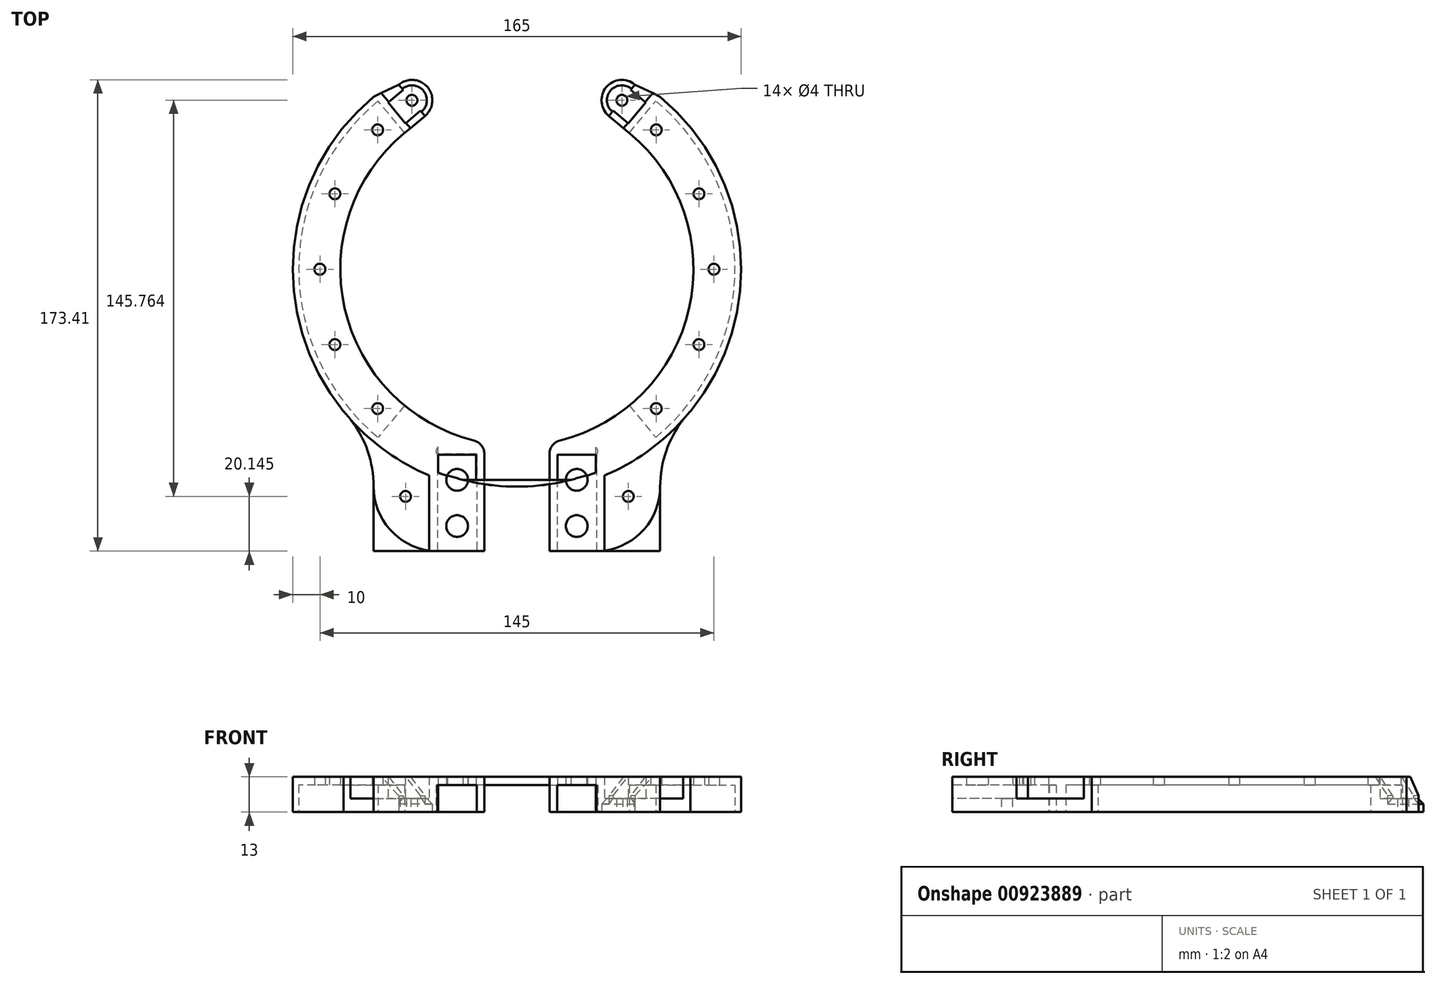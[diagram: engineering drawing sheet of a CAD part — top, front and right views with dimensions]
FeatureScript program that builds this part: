
annotation { "Feature Type Name" : "Feature", "Feature Type Description" : "" }
export const myFeature = defineFeature(function(context is Context, id is Id, definition is map)
    precondition{}
    {
        {
            var Q0;
            Q0=qCreatedBy(makeId("Top.planeOp"),FACE);
            var sketch = newSketch(context, id + "F0", { "sketchPlane" : qUnion([Q0])});
            skArc(sketch, "E0", {"start": v(-55.64, 25) * mm, "mid": v(-61, 0) * mm, "end": v(-55.64, -25) * mm});
            skArc(sketch, "E1.trimOffspring", {"start": v(55.64, -25) * mm, "mid": v(61, 0) * mm, "end": v(55.64, 25) * mm});
            skCircle(sketch, "E2", {"center": v(0, 0) * mm, "radius": 61 * mm});
            skCircle(sketch, "E3", {"center": v(0, 0) * mm, "radius": 65 * mm});
            skLineSegment(sketch, "E4", {"start": v(-41.53, 50) * mm, "end": v(-41.53, -50) * mm});
            skCircle(sketch, "E5", {"center": v(0, 0) * mm, "radius": 80 * mm});
            skLineSegment(sketch, "E6", {"start": v(-41.53, 50) * mm, "end": v(-51.12, 61.54) * mm});
            skLineSegment(sketch, "E7", {"start": v(-41.53, -50) * mm, "end": v(-51.12, -61.54) * mm});
            skArc(sketch, "E8", {"start": v(-46.33, -55.77) * mm, "mid": v(-72.5, 0) * mm, "end": v(-46.33, 55.77) * mm});
            skCircle(sketch, "E9", {"center": v(-72.5, 0) * mm, "radius": 2 * mm});
            skCircle(sketch, "E10.1.0", {"center": v(-66.98, -27.74) * mm, "radius": 2 * mm});
            skCircle(sketch, "E10.2.0", {"center": v(-51.27, -51.27) * mm, "radius": 2 * mm});
            skCircle(sketch, "E11.1.3.0", {"center": v(-27.74, -66.98) * mm, "radius": 2 * mm});
            skCircle(sketch, "E11.1.4.0", {"center": v(0, -72.5) * mm, "radius": 2 * mm});
            skCircle(sketch, "E11.1.5.0", {"center": v(27.74, -66.98) * mm, "radius": 2 * mm});
            skCircle(sketch, "E11.1.6.0", {"center": v(51.27, -51.27) * mm, "radius": 2 * mm});
            skCircle(sketch, "E11.1.7.0", {"center": v(66.98, -27.74) * mm, "radius": 2 * mm});
            skCircle(sketch, "E12.1.8.0", {"center": v(72.5, 0) * mm, "radius": 2 * mm});
            skCircle(sketch, "E12.1.9.0", {"center": v(66.98, 27.74) * mm, "radius": 2 * mm});
            skCircle(sketch, "E12.1.10.0", {"center": v(51.27, 51.27) * mm, "radius": 2 * mm});
            skCircle(sketch, "E12.1.11.0", {"center": v(27.74, 66.98) * mm, "radius": 2 * mm});
            skCircle(sketch, "E13.1.12.0", {"center": v(0, 72.5) * mm, "radius": 2 * mm});
            skCircle(sketch, "E13.1.13.0", {"center": v(-27.74, 66.98) * mm, "radius": 2 * mm});
            skCircle(sketch, "E13.1.14.0", {"center": v(-51.27, 51.27) * mm, "radius": 2 * mm});
            skCircle(sketch, "E13.1.15.0", {"center": v(-66.98, 27.74) * mm, "radius": 2 * mm});
            skLineSegment(sketch, "E14", {"start": v(-51.12, 61.54) * mm, "end": v(-43.43, 67.93) * mm});
            skLineSegment(sketch, "E15", {"start": v(-43.43, 67.93) * mm, "end": v(-33.84, 56.39) * mm});
            skLineSegment(sketch, "E16", {"start": v(-33.84, 56.39) * mm, "end": v(-41.53, 50) * mm});
            skArc(sketch, "E17", {"start": v(-43.43, 67.93) * mm, "mid": v(-32.86, 66.95) * mm, "end": v(-33.84, 56.39) * mm});
            skCircle(sketch, "E18", {"center": v(-38.63, 62.16) * mm, "radius": 2 * mm});
            skLineSegment(sketch, "E19.0", {"start": v(-35.44, 58.31) * mm, "end": v(-43.13, 51.92) * mm});
            skLineSegment(sketch, "E20.0", {"start": v(-49.52, 59.62) * mm, "end": v(-41.83, 66) * mm});
            skLineSegment(sketch, "E21", {"start": v(-51.12, 61.54) * mm, "end": v(-52.72, 63.46) * mm});
            skLineSegment(sketch, "E22", {"start": v(-51.12, -61.54) * mm, "end": v(-52.72, -63.46) * mm});
            skArc(sketch, "E23", {"start": v(-52.72, -63.46) * mm, "mid": v(-82.5, 0) * mm, "end": v(-52.72, 63.46) * mm});
            skLineSegment(sketch, "E24", {"start": v(-52.72, 63.46) * mm, "end": v(-43.43, 67.93) * mm});
            skLineSegment(sketch, "E25.bottom", {"start": v(22, -77.5) * mm, "end": v(-22, -77.5) * mm});
            skLineSegment(sketch, "E25.top", {"start": v(22, -94.5) * mm, "end": v(-22, -94.5) * mm});
            skLineSegment(sketch, "E25.left", {"start": v(22, -77.5) * mm, "end": v(22, -94.5) * mm});
            skLineSegment(sketch, "E25.right", {"start": v(-22, -77.5) * mm, "end": v(-22, -94.5) * mm});
            skPoint(sketch, "E25.middle", {"position": v(0, -86) * mm});
            skCircle(sketch, "E26", {"center": v(-22, -77.5) * mm, "radius": 4 * mm});
            skCircle(sketch, "E27", {"center": v(-22, -94.5) * mm, "radius": 4 * mm});
            skLineSegment(sketch, "E28.bottom", {"start": v(-15, -68.25) * mm, "end": v(-29, -68.25) * mm});
            skLineSegment(sketch, "E28.top", {"start": v(-15, -103.75) * mm, "end": v(-29, -103.75) * mm});
            skLineSegment(sketch, "E28.left", {"start": v(-15, -68.25) * mm, "end": v(-15, -103.75) * mm});
            skLineSegment(sketch, "E28.right", {"start": v(-29, -68.25) * mm, "end": v(-29, -103.75) * mm});
            skPoint(sketch, "E28.middle", {"position": v(-22, -86) * mm});
            skLineSegment(sketch, "E29.bottom", {"start": v(-29, -103.75) * mm, "end": v(-52.72, -103.75) * mm});
            skLineSegment(sketch, "E29.top", {"start": v(-29, -63.46) * mm, "end": v(-52.72, -63.46) * mm});
            skLineSegment(sketch, "E29.left", {"start": v(-29, -103.75) * mm, "end": v(-29, -63.46) * mm});
            skLineSegment(sketch, "E29.right", {"start": v(-52.72, -103.75) * mm, "end": v(-52.72, -63.46) * mm});
            skArc(sketch, "E30", {"start": v(-29, -103.75) * mm, "mid": v(-45.77, -96.8) * mm, "end": v(-52.72, -80.03) * mm});
            skLineSegment(sketch, "E31", {"start": v(-52.72, -80.03) * mm, "end": v(-29, -80.03) * mm, "construction": true});
            skArc(sketch, "E32", {"start": v(-52.72, -80.03) * mm, "mid": v(-55.58, -65.13) * mm, "end": v(-63.77, -52.34) * mm});
            skLineSegment(sketch, "E33", {"start": v(-15, -103.75) * mm, "end": v(-12, -103.75) * mm});
            skLineSegment(sketch, "E34", {"start": v(-12, -103.75) * mm, "end": v(-12, -63.88) * mm});
            skLineSegment(sketch, "E35.0", {"start": v(-14.75, -68) * mm, "end": v(-14.75, -103.75) * mm});
            skLineSegment(sketch, "E35.1", {"start": v(-14.75, -68) * mm, "end": v(-29.25, -68) * mm});
            skLineSegment(sketch, "E35.2", {"start": v(-29.25, -68) * mm, "end": v(-29.25, -103.75) * mm});
            skLineSegment(sketch, "E36.0", {"start": v(-32.25, -75.94) * mm, "end": v(-32.25, -103.53) * mm});
            skArc(sketch, "E37", {"start": v(-52.72, -63.46) * mm, "mid": v(-42.94, -70.45) * mm, "end": v(-32.25, -75.94) * mm});
            skLineSegment(sketch, "E38", {"start": v(-29.25, -103.75) * mm, "end": v(-40.98, -83.6) * mm, "construction": true});
            skLineSegment(sketch, "E39", {"start": v(-40.98, -83.6) * mm, "end": v(-52.72, -63.46) * mm, "construction": true});
            skCircle(sketch, "E40", {"center": v(-40.98, -83.6) * mm, "radius": 2 * mm});
            skLineSegment(sketch, "E41.0", {"start": v(-41.34, -50.16) * mm, "end": v(-51.08, -61.9) * mm});
            skCircle(sketch, "E42.0", {"center": v(0, 0) * mm, "radius": 80.25 * mm});
            skLineSegment(sketch, "E43.0", {"start": v(-41.34, 50.16) * mm, "end": v(-51.08, 61.9) * mm});
            skLineSegment(sketch, "E44.0", {"start": v(-39.38, 51.71) * mm, "end": v(-49.13, 63.45) * mm});
            skSolve(sketch);
        }
        {
            var Q0;
            {var subQ0=sQuery(id+"F0.wireOp",EDGE,"E8");var subQ1=sQuery(id+"F0.wireOp",EDGE,"E6");var subQ2=makeQuery(id+"F0.imprint","INTERSECT",VERTEX,{"derivedFrom":[subQ1,subQ0]});Q0=makeQuery(id+"F0.imprint","IMPRINT",FACE,{"disambiguationData":[TD([[makeQuery(id+"F0.imprint","IMPRINT",EDGE,{"disambiguationData":[TD([[subQ2,1.0]])],"derivedFrom":subQ1}),1.0]])]});}
            var Q1;
            {var subQ1=sQuery(id+"F0.wireOp",EDGE,"E8");var subQ14=sQuery(id+"F0.wireOp",EDGE,"E6");var subQ18=makeQuery(id+"F0.imprint","INTERSECT",VERTEX,{"derivedFrom":[subQ14,subQ1]});Q1=makeQuery(id+"F0.imprint","IMPRINT",FACE,{"disambiguationData":[TD([[makeQuery(id+"F0.imprint","IMPRINT",EDGE,{"disambiguationData":[TD([[subQ18,-1.0]])],"derivedFrom":subQ14}),1.0]])]});}
            var Q2;
            {var subQ0=sQuery(id+"F0.wireOp",EDGE,"E21");var subQ5=sQuery(id+"F0.wireOp",EDGE,"E42.0");var subQ6=makeQuery(id+"F0.imprint","INTERSECT",VERTEX,{"derivedFrom":[subQ0,subQ5]});Q2=makeQuery(id+"F0.imprint","IMPRINT",FACE,{"disambiguationData":[TD([[makeQuery(id+"F0.imprint","IMPRINT",EDGE,{"disambiguationData":[TD([[subQ6,-1.0]])],"derivedFrom":subQ5}),1.0]])]});}
            var Q3;
            {var subQ0=sQuery(id+"F0.wireOp",EDGE,"E23");var subQ3=sQuery(id+"F0.wireOp",EDGE,"E32");var subQ5=makeQuery(id+"F0.imprint","INTERSECT",VERTEX,{"disambiguationData":[OD(0.0)],"derivedFrom":[subQ0,subQ3]});Q3=makeQuery(id+"F0.imprint","IMPRINT",FACE,{"disambiguationData":[TD([[makeQuery(id+"F0.imprint","IMPRINT",EDGE,{"disambiguationData":[TD([[subQ5,1.0]])],"derivedFrom":subQ3}),-1.0]])]});}
            var Q4;
            {var subQ1=sQuery(id+"F0.wireOp",EDGE,"E15");var subQ3=sQuery(id+"F0.wireOp",EDGE,"E19.0");var subQ4=makeQuery(id+"F0.imprint","INTERSECT",VERTEX,{"derivedFrom":[subQ1,subQ3]});Q4=makeQuery(id+"F0.imprint","IMPRINT",FACE,{"disambiguationData":[TD([[makeQuery(id+"F0.imprint","IMPRINT",EDGE,{"disambiguationData":[TD([[subQ4,-1.0]])],"derivedFrom":subQ3}),1.0]])]});}
            var Q5;
            {var subQ0=sQuery(id+"F0.wireOp",EDGE,"E15");var subQ1=sQuery(id+"F0.wireOp",EDGE,"E5");var subQ2=makeQuery(id+"F0.imprint","INTERSECT",VERTEX,{"derivedFrom":[subQ1,subQ0]});Q5=makeQuery(id+"F0.imprint","IMPRINT",FACE,{"disambiguationData":[TD([[makeQuery(id+"F0.imprint","IMPRINT",EDGE,{"disambiguationData":[TD([[subQ2,-1.0]])],"derivedFrom":subQ1}),1.0]])]});}
            var Q6;
            {var subQ4=sQuery(id+"F0.wireOp",EDGE,"E24");Q6=makeQuery(id+"F0.imprint","IMPRINT",FACE,{"disambiguationData":[TD([[makeQuery(id+"F0.imprint","IMPRINT",EDGE,{"derivedFrom":subQ4}),-1.0]])]});}
            var Q7;
            {var subQ0=sQuery(id+"F0.wireOp",EDGE,"E43.0");var subQ1=sQuery(id+"F0.wireOp",EDGE,"E14");var subQ2=makeQuery(id+"F0.imprint","INTERSECT",VERTEX,{"derivedFrom":[subQ1,subQ0]});Q7=makeQuery(id+"F0.imprint","IMPRINT",FACE,{"disambiguationData":[TD([[makeQuery(id+"F0.imprint","IMPRINT",EDGE,{"disambiguationData":[TD([[subQ2,-1.0]])],"derivedFrom":subQ1}),1.0]])]});}
            var Q8;
            {var subQ3=sQuery(id+"F0.wireOp",EDGE,"E43.0");var subQ5=sQuery(id+"F0.wireOp",EDGE,"E42.0");var subQ7=makeQuery(id+"F0.imprint","INTERSECT",VERTEX,{"derivedFrom":[subQ5,subQ3]});Q8=makeQuery(id+"F0.imprint","IMPRINT",FACE,{"disambiguationData":[TD([[makeQuery(id+"F0.imprint","IMPRINT",EDGE,{"disambiguationData":[TD([[subQ7,-1.0]])],"derivedFrom":subQ5}),1.0]])]});}
            var Q9;
            {var subQ0=sQuery(id+"F0.wireOp",EDGE,"E6");var subQ5=sQuery(id+"F0.wireOp",EDGE,"E20.0");var subQ6=makeQuery(id+"F0.imprint","INTERSECT",VERTEX,{"derivedFrom":[subQ0,subQ5]});Q9=makeQuery(id+"F0.imprint","IMPRINT",FACE,{"disambiguationData":[TD([[makeQuery(id+"F0.imprint","IMPRINT",EDGE,{"disambiguationData":[TD([[subQ6,-1.0]])],"derivedFrom":subQ5}),1.0]])]});}
            var Q10;
            {var subQ1=sQuery(id+"F0.wireOp",EDGE,"E6");var subQ5=makeQuery(id+"F0.imprint","INTERSECT",VERTEX,{"derivedFrom":[subQ1,sQuery(id+"F0.wireOp",EDGE,"E8")]});Q10=makeQuery(id+"F0.imprint","IMPRINT",FACE,{"disambiguationData":[TD([[makeQuery(id+"F0.imprint","IMPRINT",EDGE,{"disambiguationData":[TD([[subQ5,1.0]])],"derivedFrom":subQ1}),-1.0]])]});}
            var Q11;
            {var subQ1=sQuery(id+"F0.wireOp",EDGE,"E6");var subQ3=sQuery(id+"F0.wireOp",EDGE,"E19.0");var subQ4=makeQuery(id+"F0.imprint","INTERSECT",VERTEX,{"derivedFrom":[subQ1,subQ3]});Q11=makeQuery(id+"F0.imprint","IMPRINT",FACE,{"disambiguationData":[TD([[makeQuery(id+"F0.imprint","IMPRINT",EDGE,{"disambiguationData":[TD([[subQ4,1.0]])],"derivedFrom":subQ3}),1.0]])]});}
            var Q12;
            {var subQ1=sQuery(id+"F0.wireOp",EDGE,"E14");var subQ3=sQuery(id+"F0.wireOp",EDGE,"E42.0");var subQ4=makeQuery(id+"F0.imprint","INTERSECT",VERTEX,{"derivedFrom":[subQ1,subQ3]});Q12=makeQuery(id+"F0.imprint","IMPRINT",FACE,{"disambiguationData":[TD([[makeQuery(id+"F0.imprint","IMPRINT",EDGE,{"disambiguationData":[TD([[subQ4,1.0]])],"derivedFrom":subQ3}),-1.0]])]});}
            var Q13;
            {var subQ0=sQuery(id+"F0.wireOp",EDGE,"E15");var subQ1=sQuery(id+"F0.wireOp",EDGE,"E5");var subQ2=makeQuery(id+"F0.imprint","INTERSECT",VERTEX,{"derivedFrom":[subQ1,subQ0]});Q13=makeQuery(id+"F0.imprint","IMPRINT",FACE,{"disambiguationData":[TD([[makeQuery(id+"F0.imprint","IMPRINT",EDGE,{"disambiguationData":[TD([[subQ2,-1.0]])],"derivedFrom":subQ1}),-1.0]])]});}
            var Q14;
            {var subQ3=sQuery(id+"F0.wireOp",EDGE,"E5");var subQ20=makeQuery(id+"F0.imprint","INTERSECT",VERTEX,{"derivedFrom":[subQ3,sQuery(id+"F0.wireOp",EDGE,"E41.0")]});Q14=makeQuery(id+"F0.imprint","IMPRINT",FACE,{"disambiguationData":[TD([[makeQuery(id+"F0.imprint","IMPRINT",EDGE,{"disambiguationData":[TD([[subQ20,-1.0]])],"derivedFrom":subQ3}),1.0]])]});}
            var Q15;
            {var subQ0=sQuery(id+"F0.wireOp",EDGE,"E34");var subQ1=sQuery(id+"F0.wireOp",EDGE,"E25.top");var subQ2=makeQuery(id+"F0.imprint","INTERSECT",VERTEX,{"derivedFrom":[subQ1,subQ0]});Q15=makeQuery(id+"F0.imprint","IMPRINT",FACE,{"disambiguationData":[TD([[makeQuery(id+"F0.imprint","IMPRINT",EDGE,{"disambiguationData":[TD([[subQ2,-1.0]])],"derivedFrom":subQ1}),-1.0]])]});}
            var Q16;
            {var subQ0=sQuery(id+"F0.wireOp",EDGE,"E34");var subQ1=sQuery(id+"F0.wireOp",EDGE,"E25.top");var subQ2=makeQuery(id+"F0.imprint","INTERSECT",VERTEX,{"derivedFrom":[subQ1,subQ0]});Q16=makeQuery(id+"F0.imprint","IMPRINT",FACE,{"disambiguationData":[TD([[makeQuery(id+"F0.imprint","IMPRINT",EDGE,{"disambiguationData":[TD([[subQ2,-1.0]])],"derivedFrom":subQ1}),1.0]])]});}
            var Q17;
            {var subQ1=sQuery(id+"F0.wireOp",EDGE,"E5");var subQ9=sQuery(id+"F0.wireOp",EDGE,"E29.left");var subQ10=makeQuery(id+"F0.imprint","INTERSECT",VERTEX,{"derivedFrom":[subQ1,subQ9]});Q17=makeQuery(id+"F0.imprint","IMPRINT",FACE,{"disambiguationData":[TD([[makeQuery(id+"F0.imprint","IMPRINT",EDGE,{"disambiguationData":[TD([[subQ10,-1.0]])],"derivedFrom":subQ1}),1.0]])]});}
            var Q18;
            {var subQ0=sQuery(id+"F0.wireOp",EDGE,"E35.0");var subQ1=sQuery(id+"F0.wireOp",EDGE,"E5");var subQ2=makeQuery(id+"F0.imprint","INTERSECT",VERTEX,{"derivedFrom":[subQ1,subQ0]});Q18=makeQuery(id+"F0.imprint","IMPRINT",FACE,{"disambiguationData":[TD([[makeQuery(id+"F0.imprint","IMPRINT",EDGE,{"disambiguationData":[TD([[subQ2,-1.0]])],"derivedFrom":subQ1}),1.0]])]});}
            var Q19;
            {var subQ1=sQuery(id+"F0.wireOp",EDGE,"E28.bottom");var subQ3=sQuery(id+"F0.wireOp",EDGE,"E11.1.3.0");var subQ4=makeQuery(id+"F0.imprint","INTERSECT",VERTEX,{"derivedFrom":[subQ3,subQ1]});Q19=makeQuery(id+"F0.imprint","IMPRINT",FACE,{"disambiguationData":[TD([[makeQuery(id+"F0.imprint","IMPRINT",EDGE,{"disambiguationData":[TD([[subQ4,-1.0]])],"derivedFrom":subQ3}),-1.0]])]});}
            var Q20;
            {var subQ0=sQuery(id+"F0.wireOp",EDGE,"E26");var subQ1=sQuery(id+"F0.wireOp",EDGE,"E5");var subQ2=makeQuery(id+"F0.imprint","INTERSECT",VERTEX,{"disambiguationData":[OD(1.0)],"derivedFrom":[subQ1,subQ0]});Q20=makeQuery(id+"F0.imprint","IMPRINT",FACE,{"disambiguationData":[TD([[makeQuery(id+"F0.imprint","IMPRINT",EDGE,{"disambiguationData":[TD([[subQ2,-1.0]])],"derivedFrom":subQ1}),1.0]])]});}
            var Q21;
            {var subQ10=sQuery(id+"F0.wireOp",EDGE,"E28.top");Q21=makeQuery(id+"F0.imprint","IMPRINT",FACE,{"disambiguationData":[TD([[makeQuery(id+"F0.imprint","IMPRINT",EDGE,{"derivedFrom":subQ10}),-1.0]])]});}
            var Q22;
            {var subQ1=sQuery(id+"F0.wireOp",EDGE,"E25.top");var subQ8=sQuery(id+"F0.wireOp",EDGE,"E28.left");var subQ11=makeQuery(id+"F0.imprint","INTERSECT",VERTEX,{"derivedFrom":[subQ1,subQ8]});Q22=makeQuery(id+"F0.imprint","IMPRINT",FACE,{"disambiguationData":[TD([[makeQuery(id+"F0.imprint","IMPRINT",EDGE,{"disambiguationData":[TD([[subQ11,-1.0]])],"derivedFrom":subQ1}),-1.0]])]});}
            var Q23;
            {var subQ0=sQuery(id+"F0.wireOp",EDGE,"E28.left");var subQ1=sQuery(id+"F0.wireOp",EDGE,"E5");var subQ2=makeQuery(id+"F0.imprint","INTERSECT",VERTEX,{"derivedFrom":[subQ1,subQ0]});Q23=makeQuery(id+"F0.imprint","IMPRINT",FACE,{"disambiguationData":[TD([[makeQuery(id+"F0.imprint","IMPRINT",EDGE,{"disambiguationData":[TD([[subQ2,-1.0]])],"derivedFrom":subQ1}),-1.0]])]});}
            var Q24;
            {var subQ0=sQuery(id+"F0.wireOp",EDGE,"E35.0");var subQ1=sQuery(id+"F0.wireOp",EDGE,"E25.top");var subQ2=makeQuery(id+"F0.imprint","INTERSECT",VERTEX,{"derivedFrom":[subQ1,subQ0]});Q24=makeQuery(id+"F0.imprint","IMPRINT",FACE,{"disambiguationData":[TD([[makeQuery(id+"F0.imprint","IMPRINT",EDGE,{"disambiguationData":[TD([[subQ2,-1.0]])],"derivedFrom":subQ1}),-1.0]])]});}
            var Q25;
            {var subQ0=sQuery(id+"F0.wireOp",EDGE,"E35.0");var subQ1=sQuery(id+"F0.wireOp",EDGE,"E5");var subQ2=makeQuery(id+"F0.imprint","INTERSECT",VERTEX,{"derivedFrom":[subQ1,subQ0]});Q25=makeQuery(id+"F0.imprint","IMPRINT",FACE,{"disambiguationData":[TD([[makeQuery(id+"F0.imprint","IMPRINT",EDGE,{"disambiguationData":[TD([[subQ2,-1.0]])],"derivedFrom":subQ1}),-1.0]])]});}
            var Q26;
            {var subQ0=sQuery(id+"F0.wireOp",EDGE,"E28.left");var subQ1=sQuery(id+"F0.wireOp",EDGE,"E5");var subQ2=makeQuery(id+"F0.imprint","INTERSECT",VERTEX,{"derivedFrom":[subQ1,subQ0]});Q26=makeQuery(id+"F0.imprint","IMPRINT",FACE,{"disambiguationData":[TD([[makeQuery(id+"F0.imprint","IMPRINT",EDGE,{"disambiguationData":[TD([[subQ2,-1.0]])],"derivedFrom":subQ1}),1.0]])]});}
            var Q27;
            {var subQ0=sQuery(id+"F0.wireOp",EDGE,"E26");var subQ1=sQuery(id+"F0.wireOp",EDGE,"E5");var subQ2=makeQuery(id+"F0.imprint","INTERSECT",VERTEX,{"disambiguationData":[OD(1.0)],"derivedFrom":[subQ1,subQ0]});Q27=makeQuery(id+"F0.imprint","IMPRINT",FACE,{"disambiguationData":[TD([[makeQuery(id+"F0.imprint","IMPRINT",EDGE,{"disambiguationData":[TD([[subQ2,-1.0]])],"derivedFrom":subQ1}),-1.0]])]});}
            var Q28;
            {var subQ0=sQuery(id+"F0.wireOp",EDGE,"E35.0");var subQ1=sQuery(id+"F0.wireOp",EDGE,"E25.top");var subQ2=makeQuery(id+"F0.imprint","INTERSECT",VERTEX,{"derivedFrom":[subQ1,subQ0]});Q28=makeQuery(id+"F0.imprint","IMPRINT",FACE,{"disambiguationData":[TD([[makeQuery(id+"F0.imprint","IMPRINT",EDGE,{"disambiguationData":[TD([[subQ2,-1.0]])],"derivedFrom":subQ1}),1.0]])]});}
            var Q29;
            {var subQ0=sQuery(id+"F0.wireOp",EDGE,"E30");var subQ5=sQuery(id+"F0.wireOp",EDGE,"E35.2");var subQ6=makeQuery(id+"F0.imprint","INTERSECT",VERTEX,{"derivedFrom":[subQ0,subQ5]});Q29=makeQuery(id+"F0.imprint","IMPRINT",FACE,{"disambiguationData":[TD([[makeQuery(id+"F0.imprint","IMPRINT",EDGE,{"disambiguationData":[TD([[subQ6,1.0]])],"derivedFrom":subQ5}),1.0]])]});}
            var Q30;
            {var subQ4=sQuery(id+"F0.wireOp",EDGE,"E35.2");var subQ5=sQuery(id+"F0.wireOp",EDGE,"E30");var subQ6=makeQuery(id+"F0.imprint","INTERSECT",VERTEX,{"derivedFrom":[subQ5,subQ4]});Q30=makeQuery(id+"F0.imprint","IMPRINT",FACE,{"disambiguationData":[TD([[makeQuery(id+"F0.imprint","IMPRINT",EDGE,{"disambiguationData":[TD([[subQ6,-1.0]])],"derivedFrom":subQ5}),-1.0]])]});}
            var Q31;
            {var subQ0=sQuery(id+"F0.wireOp",EDGE,"E37");Q31=makeQuery(id+"F0.imprint","IMPRINT",FACE,{"disambiguationData":[TD([[makeQuery(id+"F0.imprint","IMPRINT",EDGE,{"derivedFrom":subQ0}),1.0]])]});}
            var Q32;
            {var subQ3=sQuery(id+"F0.wireOp",EDGE,"E42.0");var subQ6=makeQuery(id+"F0.imprint","INTERSECT",VERTEX,{"derivedFrom":[sQuery(id+"F0.wireOp",EDGE,"E41.0"),subQ3]});Q32=makeQuery(id+"F0.imprint","IMPRINT",FACE,{"disambiguationData":[TD([[makeQuery(id+"F0.imprint","IMPRINT",EDGE,{"disambiguationData":[TD([[subQ6,1.0]])],"derivedFrom":subQ3}),-1.0]])]});}
            var Q33;
            {var subQ0=sQuery(id+"F0.wireOp",EDGE,"E29.left");var subQ1=sQuery(id+"F0.wireOp",EDGE,"E11.1.3.0");var subQ2=makeQuery(id+"F0.imprint","INTERSECT",VERTEX,{"disambiguationData":[OD(0.0)],"derivedFrom":[subQ1,subQ0]});Q33=makeQuery(id+"F0.imprint","IMPRINT",FACE,{"disambiguationData":[TD([[makeQuery(id+"F0.imprint","IMPRINT",EDGE,{"disambiguationData":[TD([[subQ2,1.0]])],"derivedFrom":subQ1}),1.0]])]});}
            var Q34;
            {var subQ0=sQuery(id+"F0.wireOp",EDGE,"E29.left");var subQ1=sQuery(id+"F0.wireOp",EDGE,"E11.1.3.0");var subQ2=makeQuery(id+"F0.imprint","INTERSECT",VERTEX,{"disambiguationData":[OD(1.0)],"derivedFrom":[subQ1,subQ0]});Q34=makeQuery(id+"F0.imprint","IMPRINT",FACE,{"disambiguationData":[TD([[makeQuery(id+"F0.imprint","IMPRINT",EDGE,{"disambiguationData":[TD([[subQ2,-1.0]])],"derivedFrom":subQ1}),1.0]])]});}
            var Q35;
            {var subQ0=sQuery(id+"F0.wireOp",EDGE,"E35.2");var subQ1=sQuery(id+"F0.wireOp",EDGE,"E11.1.3.0");var subQ2=makeQuery(id+"F0.imprint","INTERSECT",VERTEX,{"derivedFrom":[subQ1,subQ0]});Q35=makeQuery(id+"F0.imprint","IMPRINT",FACE,{"disambiguationData":[TD([[makeQuery(id+"F0.imprint","IMPRINT",EDGE,{"disambiguationData":[TD([[subQ2,1.0]])],"derivedFrom":subQ1}),1.0]])]});}
            var Q36;
            {var subQ0=sQuery(id+"F0.wireOp",EDGE,"E28.bottom");var subQ1=sQuery(id+"F0.wireOp",EDGE,"E11.1.3.0");var subQ2=makeQuery(id+"F0.imprint","INTERSECT",VERTEX,{"derivedFrom":[subQ1,subQ0]});Q36=makeQuery(id+"F0.imprint","IMPRINT",FACE,{"disambiguationData":[TD([[makeQuery(id+"F0.imprint","IMPRINT",EDGE,{"disambiguationData":[TD([[subQ2,-1.0]])],"derivedFrom":subQ1}),1.0]])]});}
            var Q37;
            {var subQ0=sQuery(id+"F0.wireOp",EDGE,"E35.2");var subQ1=sQuery(id+"F0.wireOp",EDGE,"E5");var subQ2=makeQuery(id+"F0.imprint","INTERSECT",VERTEX,{"derivedFrom":[subQ1,subQ0]});Q37=makeQuery(id+"F0.imprint","IMPRINT",FACE,{"disambiguationData":[TD([[makeQuery(id+"F0.imprint","IMPRINT",EDGE,{"disambiguationData":[TD([[subQ2,-1.0]])],"derivedFrom":subQ1}),1.0]])]});}
            var Q38;
            {var subQ0=sQuery(id+"F0.wireOp",EDGE,"E29.left");var subQ1=sQuery(id+"F0.wireOp",EDGE,"E5");var subQ2=makeQuery(id+"F0.imprint","INTERSECT",VERTEX,{"derivedFrom":[subQ1,subQ0]});Q38=makeQuery(id+"F0.imprint","IMPRINT",FACE,{"disambiguationData":[TD([[makeQuery(id+"F0.imprint","IMPRINT",EDGE,{"disambiguationData":[TD([[subQ2,-1.0]])],"derivedFrom":subQ1}),-1.0]])]});}
            var Q39;
            {var subQ4=sQuery(id+"F0.wireOp",EDGE,"E35.2");var subQ6=sQuery(id+"F0.wireOp",EDGE,"E11.1.3.0");var subQ8=makeQuery(id+"F0.imprint","INTERSECT",VERTEX,{"derivedFrom":[subQ6,subQ4]});Q39=makeQuery(id+"F0.imprint","IMPRINT",FACE,{"disambiguationData":[TD([[makeQuery(id+"F0.imprint","IMPRINT",EDGE,{"disambiguationData":[TD([[subQ8,-1.0]])],"derivedFrom":subQ6}),1.0]])]});}
            var Q40;
            {var subQ0=sQuery(id+"F0.wireOp",EDGE,"E36.0");var subQ1=sQuery(id+"F0.wireOp",EDGE,"E5");var subQ2=makeQuery(id+"F0.imprint","INTERSECT",VERTEX,{"derivedFrom":[subQ1,subQ0]});Q40=makeQuery(id+"F0.imprint","IMPRINT",FACE,{"disambiguationData":[TD([[makeQuery(id+"F0.imprint","IMPRINT",EDGE,{"disambiguationData":[TD([[subQ2,-1.0]])],"derivedFrom":subQ1}),-1.0]])]});}
            var Q41;
            {var subQ0=sQuery(id+"F0.wireOp",EDGE,"E35.2");var subQ1=sQuery(id+"F0.wireOp",EDGE,"E5");var subQ2=makeQuery(id+"F0.imprint","INTERSECT",VERTEX,{"derivedFrom":[subQ1,subQ0]});Q41=makeQuery(id+"F0.imprint","IMPRINT",FACE,{"disambiguationData":[TD([[makeQuery(id+"F0.imprint","IMPRINT",EDGE,{"disambiguationData":[TD([[subQ2,-1.0]])],"derivedFrom":subQ1}),-1.0]])]});}
            var Q42;
            {var subQ0=sQuery(id+"F0.wireOp",EDGE,"E41.0");var subQ1=sQuery(id+"F0.wireOp",EDGE,"E5");var subQ2=makeQuery(id+"F0.imprint","INTERSECT",VERTEX,{"derivedFrom":[subQ1,subQ0]});Q42=makeQuery(id+"F0.imprint","IMPRINT",FACE,{"disambiguationData":[TD([[makeQuery(id+"F0.imprint","IMPRINT",EDGE,{"disambiguationData":[TD([[subQ2,-1.0]])],"derivedFrom":subQ1}),-1.0]])]});}
            var Q43;
            {var subQ3=sQuery(id+"F0.wireOp",EDGE,"E41.0");var subQ5=sQuery(id+"F0.wireOp",EDGE,"E42.0");var subQ6=makeQuery(id+"F0.imprint","INTERSECT",VERTEX,{"derivedFrom":[subQ3,subQ5]});Q43=makeQuery(id+"F0.imprint","IMPRINT",FACE,{"disambiguationData":[TD([[makeQuery(id+"F0.imprint","IMPRINT",EDGE,{"disambiguationData":[TD([[subQ6,1.0]])],"derivedFrom":subQ3}),-1.0]])]});}
            var Q44;
            {var subQ4=sQuery(id+"F0.wireOp",EDGE,"E3");var subQ6=sQuery(id+"F0.wireOp",EDGE,"E41.0");var subQ7=makeQuery(id+"F0.imprint","INTERSECT",VERTEX,{"derivedFrom":[subQ4,subQ6]});Q44=makeQuery(id+"F0.imprint","IMPRINT",FACE,{"disambiguationData":[TD([[makeQuery(id+"F0.imprint","IMPRINT",EDGE,{"disambiguationData":[TD([[subQ7,-1.0]])],"derivedFrom":subQ6}),-1.0]])]});}
            var Q45;
            {var subQ0=sQuery(id+"F0.wireOp",EDGE,"E44.0");var subQ1=sQuery(id+"F0.wireOp",EDGE,"E14");var subQ2=makeQuery(id+"F0.imprint","INTERSECT",VERTEX,{"derivedFrom":[subQ1,subQ0]});Q45=makeQuery(id+"F0.imprint","IMPRINT",FACE,{"disambiguationData":[TD([[makeQuery(id+"F0.imprint","IMPRINT",EDGE,{"disambiguationData":[TD([[subQ2,-1.0]])],"derivedFrom":subQ1}),1.0]])]});}
            var Q46;
            {var subQ0=sQuery(id+"F0.wireOp",EDGE,"E44.0");var subQ1=sQuery(id+"F0.wireOp",EDGE,"E5");var subQ2=makeQuery(id+"F0.imprint","INTERSECT",VERTEX,{"derivedFrom":[subQ1,subQ0]});Q46=makeQuery(id+"F0.imprint","IMPRINT",FACE,{"disambiguationData":[TD([[makeQuery(id+"F0.imprint","IMPRINT",EDGE,{"disambiguationData":[TD([[subQ2,-1.0]])],"derivedFrom":subQ1}),1.0]])]});}
            var Q47;
            {var subQ0=sQuery(id+"F0.wireOp",EDGE,"E44.0");var subQ1=sQuery(id+"F0.wireOp",EDGE,"E19.0");var subQ2=makeQuery(id+"F0.imprint","INTERSECT",VERTEX,{"derivedFrom":[subQ1,subQ0]});Q47=makeQuery(id+"F0.imprint","IMPRINT",FACE,{"disambiguationData":[TD([[makeQuery(id+"F0.imprint","IMPRINT",EDGE,{"disambiguationData":[TD([[subQ2,-1.0]])],"derivedFrom":subQ1}),-1.0]])]});}
            var Q48;
            {var subQ0=sQuery(id+"F0.wireOp",EDGE,"E44.0");var subQ1=sQuery(id+"F0.wireOp",EDGE,"E16");var subQ2=makeQuery(id+"F0.imprint","INTERSECT",VERTEX,{"derivedFrom":[subQ1,subQ0]});Q48=makeQuery(id+"F0.imprint","IMPRINT",FACE,{"disambiguationData":[TD([[makeQuery(id+"F0.imprint","IMPRINT",EDGE,{"disambiguationData":[TD([[subQ2,-1.0]])],"derivedFrom":subQ1}),-1.0]])]});}
            var Q49;
            {var subQ1=sQuery(id+"F0.wireOp",EDGE,"E29.top");var subQ7=sQuery(id+"F0.wireOp",EDGE,"E5");var subQ8=makeQuery(id+"F0.imprint","INTERSECT",VERTEX,{"derivedFrom":[subQ7,subQ1]});Q49=makeQuery(id+"F0.imprint","IMPRINT",FACE,{"disambiguationData":[TD([[makeQuery(id+"F0.imprint","IMPRINT",EDGE,{"disambiguationData":[TD([[subQ8,-1.0]])],"derivedFrom":subQ7}),1.0]])]});}
            var Q50;
            {var subQ0=sQuery(id+"F0.wireOp",EDGE,"E44.0");var subQ1=sQuery(id+"F0.wireOp",EDGE,"E5");var subQ2=makeQuery(id+"F0.imprint","INTERSECT",VERTEX,{"derivedFrom":[subQ1,subQ0]});Q50=makeQuery(id+"F0.imprint","IMPRINT",FACE,{"disambiguationData":[TD([[makeQuery(id+"F0.imprint","IMPRINT",EDGE,{"disambiguationData":[TD([[subQ2,-1.0]])],"derivedFrom":subQ1}),-1.0]])]});}
            var Q51;
            {var subQ3=sQuery(id+"F0.wireOp",EDGE,"E41.0");var subQ5=sQuery(id+"F0.wireOp",EDGE,"E42.0");var subQ7=makeQuery(id+"F0.imprint","INTERSECT",VERTEX,{"derivedFrom":[subQ3,subQ5]});Q51=makeQuery(id+"F0.imprint","IMPRINT",FACE,{"disambiguationData":[TD([[makeQuery(id+"F0.imprint","IMPRINT",EDGE,{"disambiguationData":[TD([[subQ7,1.0]])],"derivedFrom":subQ3}),-1.0]])]});}
            var Q52;
            {var subQ0=sQuery(id+"F0.wireOp",EDGE,"E41.0");var subQ1=sQuery(id+"F0.wireOp",EDGE,"E5");var subQ2=makeQuery(id+"F0.imprint","INTERSECT",VERTEX,{"derivedFrom":[subQ1,subQ0]});Q52=makeQuery(id+"F0.imprint","IMPRINT",FACE,{"disambiguationData":[TD([[makeQuery(id+"F0.imprint","IMPRINT",EDGE,{"disambiguationData":[TD([[subQ2,-1.0]])],"derivedFrom":subQ1}),-1.0]])]});}
            var Q53;
            {var subQ0=sQuery(id+"F0.wireOp",EDGE,"E29.top");var subQ1=sQuery(id+"F0.wireOp",EDGE,"E5");var subQ2=makeQuery(id+"F0.imprint","INTERSECT",VERTEX,{"derivedFrom":[subQ1,subQ0]});Q53=makeQuery(id+"F0.imprint","IMPRINT",FACE,{"disambiguationData":[TD([[makeQuery(id+"F0.imprint","IMPRINT",EDGE,{"disambiguationData":[TD([[subQ2,-1.0]])],"derivedFrom":subQ1}),-1.0]])]});}
            var Q54;
            {var subQ0=sQuery(id+"F0.wireOp",EDGE,"E35.2");var subQ1=sQuery(id+"F0.wireOp",EDGE,"E5");var subQ2=makeQuery(id+"F0.imprint","INTERSECT",VERTEX,{"derivedFrom":[subQ1,subQ0]});Q54=makeQuery(id+"F0.imprint","IMPRINT",FACE,{"disambiguationData":[TD([[makeQuery(id+"F0.imprint","IMPRINT",EDGE,{"disambiguationData":[TD([[subQ2,-1.0]])],"derivedFrom":subQ1}),-1.0]])]});}
            var Q55;
            {var subQ0=sQuery(id+"F0.wireOp",EDGE,"E29.left");var subQ1=sQuery(id+"F0.wireOp",EDGE,"E5");var subQ2=makeQuery(id+"F0.imprint","INTERSECT",VERTEX,{"derivedFrom":[subQ1,subQ0]});Q55=makeQuery(id+"F0.imprint","IMPRINT",FACE,{"disambiguationData":[TD([[makeQuery(id+"F0.imprint","IMPRINT",EDGE,{"disambiguationData":[TD([[subQ2,-1.0]])],"derivedFrom":subQ1}),-1.0]])]});}
            var Q56;
            {var subQ0=sQuery(id+"F0.wireOp",EDGE,"E26");var subQ1=sQuery(id+"F0.wireOp",EDGE,"E5");var subQ2=makeQuery(id+"F0.imprint","INTERSECT",VERTEX,{"disambiguationData":[OD(1.0)],"derivedFrom":[subQ1,subQ0]});Q56=makeQuery(id+"F0.imprint","IMPRINT",FACE,{"disambiguationData":[TD([[makeQuery(id+"F0.imprint","IMPRINT",EDGE,{"disambiguationData":[TD([[subQ2,-1.0]])],"derivedFrom":subQ1}),-1.0]])]});}
            var Q57;
            {var subQ0=sQuery(id+"F0.wireOp",EDGE,"E28.left");var subQ1=sQuery(id+"F0.wireOp",EDGE,"E5");var subQ2=makeQuery(id+"F0.imprint","INTERSECT",VERTEX,{"derivedFrom":[subQ1,subQ0]});Q57=makeQuery(id+"F0.imprint","IMPRINT",FACE,{"disambiguationData":[TD([[makeQuery(id+"F0.imprint","IMPRINT",EDGE,{"disambiguationData":[TD([[subQ2,-1.0]])],"derivedFrom":subQ1}),-1.0]])]});}
            var Q58;
            {var subQ0=sQuery(id+"F0.wireOp",EDGE,"E35.0");var subQ1=sQuery(id+"F0.wireOp",EDGE,"E5");var subQ2=makeQuery(id+"F0.imprint","INTERSECT",VERTEX,{"derivedFrom":[subQ1,subQ0]});Q58=makeQuery(id+"F0.imprint","IMPRINT",FACE,{"disambiguationData":[TD([[makeQuery(id+"F0.imprint","IMPRINT",EDGE,{"disambiguationData":[TD([[subQ2,-1.0]])],"derivedFrom":subQ1}),-1.0]])]});}
            extrude(context, id + "F1", {"entities" : qUnion([Q0, Q1, Q2, Q3, Q4, Q5, Q6, Q7, Q8, Q9, Q10, Q11, Q12, Q13, Q14, Q15, Q16, Q17, Q18, Q19, Q20, Q21, Q22, Q23, Q24, Q25, Q26, Q27, Q28, Q29, Q30, Q31, Q32, Q33, Q34, Q35, Q36, Q37, Q38, Q39, Q40, Q41, Q42, Q43, Q44, Q45, Q46, Q47, Q48, Q49, Q50, Q51, Q52, Q53, Q54, Q55, Q56, Q57, Q58]), "depth" : 13 * mm, "offsetDistance" : 25 * mm});
        }
        {
            var Q0;
            {var subQ1=sQuery(id+"F0.wireOp",EDGE,"E15");var subQ5=sQuery(id+"F0.wireOp",EDGE,"E20.0");var subQ6=makeQuery(id+"F0.imprint","INTERSECT",VERTEX,{"derivedFrom":[subQ1,subQ5]});Q0=makeQuery(id+"F0.imprint","IMPRINT",FACE,{"disambiguationData":[TD([[makeQuery(id+"F0.imprint","IMPRINT",EDGE,{"disambiguationData":[TD([[subQ6,-1.0]])],"derivedFrom":subQ1}),-1.0]])]});}
            var Q1;
            {var subQ0=sQuery(id+"F0.wireOp",EDGE,"E15");var subQ5=sQuery(id+"F0.wireOp",EDGE,"E5");var subQ6=makeQuery(id+"F0.imprint","INTERSECT",VERTEX,{"derivedFrom":[subQ5,subQ0]});Q1=makeQuery(id+"F0.imprint","IMPRINT",FACE,{"disambiguationData":[TD([[makeQuery(id+"F0.imprint","IMPRINT",EDGE,{"disambiguationData":[TD([[subQ6,1.0]])],"derivedFrom":subQ5}),1.0]])]});}
            var Q2;
            {var subQ0=sQuery(id+"F0.wireOp",EDGE,"E17");var subQ3=sQuery(id+"F0.wireOp",EDGE,"E42.0");var subQ5=makeQuery(id+"F0.imprint","INTERSECT",VERTEX,{"derivedFrom":[subQ0,subQ3]});Q2=makeQuery(id+"F0.imprint","IMPRINT",FACE,{"disambiguationData":[TD([[makeQuery(id+"F0.imprint","IMPRINT",EDGE,{"disambiguationData":[TD([[subQ5,-1.0]])],"derivedFrom":subQ3}),-1.0]])]});}
            var Q3;
            {var subQ0=sQuery(id+"F0.wireOp",EDGE,"E15");var subQ1=sQuery(id+"F0.wireOp",EDGE,"E5");var subQ2=makeQuery(id+"F0.imprint","INTERSECT",VERTEX,{"derivedFrom":[subQ1,subQ0]});Q3=makeQuery(id+"F0.imprint","IMPRINT",FACE,{"disambiguationData":[TD([[makeQuery(id+"F0.imprint","IMPRINT",EDGE,{"disambiguationData":[TD([[subQ2,1.0]])],"derivedFrom":subQ1}),-1.0]])]});}
            var Q4;
            {var subQ0=sQuery(id+"F0.wireOp",EDGE,"E37");Q4=makeQuery(id+"F0.imprint","IMPRINT",FACE,{"disambiguationData":[TD([[makeQuery(id+"F0.imprint","IMPRINT",EDGE,{"derivedFrom":subQ0}),-1.0]])]});}
            var Q5;
            {var subQ1=sQuery(id+"F0.wireOp",EDGE,"E23");var subQ3=sQuery(id+"F0.wireOp",EDGE,"E32");var subQ4=makeQuery(id+"F0.imprint","INTERSECT",VERTEX,{"disambiguationData":[OD(1.0)],"derivedFrom":[subQ1,subQ3]});Q5=makeQuery(id+"F0.imprint","IMPRINT",FACE,{"disambiguationData":[TD([[makeQuery(id+"F0.imprint","IMPRINT",EDGE,{"disambiguationData":[TD([[subQ4,1.0]])],"derivedFrom":subQ3}),-1.0]])]});}
            extrude(context, id + "F2", {"entities" : qUnion([Q0, Q1, Q2, Q3, Q4, Q5]), "operationType" : NewBodyOperationType.ADD, "depth" : 5 * mm, "offsetDistance" : 25 * mm});
        }
        {
            var Q0;
            {var subQ10=sQuery(id+"F0.wireOp",EDGE,"E28.top");Q0=makeQuery(id+"F0.imprint","IMPRINT",FACE,{"disambiguationData":[TD([[makeQuery(id+"F0.imprint","IMPRINT",EDGE,{"derivedFrom":subQ10}),-1.0]])]});}
            var Q1;
            {var subQ0=sQuery(id+"F0.wireOp",EDGE,"E30");var subQ5=sQuery(id+"F0.wireOp",EDGE,"E35.2");var subQ6=makeQuery(id+"F0.imprint","INTERSECT",VERTEX,{"derivedFrom":[subQ0,subQ5]});Q1=makeQuery(id+"F0.imprint","IMPRINT",FACE,{"disambiguationData":[TD([[makeQuery(id+"F0.imprint","IMPRINT",EDGE,{"disambiguationData":[TD([[subQ6,1.0]])],"derivedFrom":subQ5}),1.0]])]});}
            var Q2;
            {var subQ0=sQuery(id+"F0.wireOp",EDGE,"E35.0");var subQ1=sQuery(id+"F0.wireOp",EDGE,"E25.top");var subQ2=makeQuery(id+"F0.imprint","INTERSECT",VERTEX,{"derivedFrom":[subQ1,subQ0]});Q2=makeQuery(id+"F0.imprint","IMPRINT",FACE,{"disambiguationData":[TD([[makeQuery(id+"F0.imprint","IMPRINT",EDGE,{"disambiguationData":[TD([[subQ2,-1.0]])],"derivedFrom":subQ1}),1.0]])]});}
            var Q3;
            {var subQ1=sQuery(id+"F0.wireOp",EDGE,"E5");var subQ9=sQuery(id+"F0.wireOp",EDGE,"E29.left");var subQ10=makeQuery(id+"F0.imprint","INTERSECT",VERTEX,{"derivedFrom":[subQ1,subQ9]});Q3=makeQuery(id+"F0.imprint","IMPRINT",FACE,{"disambiguationData":[TD([[makeQuery(id+"F0.imprint","IMPRINT",EDGE,{"disambiguationData":[TD([[subQ10,-1.0]])],"derivedFrom":subQ1}),1.0]])]});}
            var Q4;
            {var subQ1=sQuery(id+"F0.wireOp",EDGE,"E25.top");var subQ9=sQuery(id+"F0.wireOp",EDGE,"E28.left");var subQ10=makeQuery(id+"F0.imprint","INTERSECT",VERTEX,{"derivedFrom":[subQ1,subQ9]});Q4=makeQuery(id+"F0.imprint","IMPRINT",FACE,{"disambiguationData":[TD([[makeQuery(id+"F0.imprint","IMPRINT",EDGE,{"disambiguationData":[TD([[subQ10,-1.0]])],"derivedFrom":subQ1}),-1.0]])]});}
            var Q5;
            {var subQ0=sQuery(id+"F0.wireOp",EDGE,"E26");var subQ1=sQuery(id+"F0.wireOp",EDGE,"E5");var subQ2=makeQuery(id+"F0.imprint","INTERSECT",VERTEX,{"disambiguationData":[OD(1.0)],"derivedFrom":[subQ1,subQ0]});Q5=makeQuery(id+"F0.imprint","IMPRINT",FACE,{"disambiguationData":[TD([[makeQuery(id+"F0.imprint","IMPRINT",EDGE,{"disambiguationData":[TD([[subQ2,-1.0]])],"derivedFrom":subQ1}),-1.0]])]});}
            var Q6;
            {var subQ0=sQuery(id+"F0.wireOp",EDGE,"E26");var subQ1=sQuery(id+"F0.wireOp",EDGE,"E5");var subQ2=makeQuery(id+"F0.imprint","INTERSECT",VERTEX,{"disambiguationData":[OD(1.0)],"derivedFrom":[subQ1,subQ0]});Q6=makeQuery(id+"F0.imprint","IMPRINT",FACE,{"disambiguationData":[TD([[makeQuery(id+"F0.imprint","IMPRINT",EDGE,{"disambiguationData":[TD([[subQ2,-1.0]])],"derivedFrom":subQ1}),1.0]])]});}
            var Q7;
            {var subQ0=sQuery(id+"F0.wireOp",EDGE,"E29.left");var subQ1=sQuery(id+"F0.wireOp",EDGE,"E5");var subQ2=makeQuery(id+"F0.imprint","INTERSECT",VERTEX,{"derivedFrom":[subQ1,subQ0]});Q7=makeQuery(id+"F0.imprint","IMPRINT",FACE,{"disambiguationData":[TD([[makeQuery(id+"F0.imprint","IMPRINT",EDGE,{"disambiguationData":[TD([[subQ2,-1.0]])],"derivedFrom":subQ1}),-1.0]])]});}
            var Q8;
            {var subQ0=sQuery(id+"F0.wireOp",EDGE,"E35.2");var subQ1=sQuery(id+"F0.wireOp",EDGE,"E5");var subQ2=makeQuery(id+"F0.imprint","INTERSECT",VERTEX,{"derivedFrom":[subQ1,subQ0]});Q8=makeQuery(id+"F0.imprint","IMPRINT",FACE,{"disambiguationData":[TD([[makeQuery(id+"F0.imprint","IMPRINT",EDGE,{"disambiguationData":[TD([[subQ2,-1.0]])],"derivedFrom":subQ1}),1.0]])]});}
            var Q9;
            {var subQ0=sQuery(id+"F0.wireOp",EDGE,"E35.2");var subQ1=sQuery(id+"F0.wireOp",EDGE,"E5");var subQ2=makeQuery(id+"F0.imprint","INTERSECT",VERTEX,{"derivedFrom":[subQ1,subQ0]});Q9=makeQuery(id+"F0.imprint","IMPRINT",FACE,{"disambiguationData":[TD([[makeQuery(id+"F0.imprint","IMPRINT",EDGE,{"disambiguationData":[TD([[subQ2,-1.0]])],"derivedFrom":subQ1}),-1.0]])]});}
            var Q10;
            {var subQ1=sQuery(id+"F0.wireOp",EDGE,"E28.bottom");var subQ3=sQuery(id+"F0.wireOp",EDGE,"E11.1.3.0");var subQ4=makeQuery(id+"F0.imprint","INTERSECT",VERTEX,{"derivedFrom":[subQ3,subQ1]});Q10=makeQuery(id+"F0.imprint","IMPRINT",FACE,{"disambiguationData":[TD([[makeQuery(id+"F0.imprint","IMPRINT",EDGE,{"disambiguationData":[TD([[subQ4,-1.0]])],"derivedFrom":subQ3}),-1.0]])]});}
            var Q11;
            {var subQ0=sQuery(id+"F0.wireOp",EDGE,"E28.left");var subQ1=sQuery(id+"F0.wireOp",EDGE,"E5");var subQ2=makeQuery(id+"F0.imprint","INTERSECT",VERTEX,{"derivedFrom":[subQ1,subQ0]});Q11=makeQuery(id+"F0.imprint","IMPRINT",FACE,{"disambiguationData":[TD([[makeQuery(id+"F0.imprint","IMPRINT",EDGE,{"disambiguationData":[TD([[subQ2,-1.0]])],"derivedFrom":subQ1}),1.0]])]});}
            var Q12;
            {var subQ0=sQuery(id+"F0.wireOp",EDGE,"E35.0");var subQ1=sQuery(id+"F0.wireOp",EDGE,"E25.top");var subQ2=makeQuery(id+"F0.imprint","INTERSECT",VERTEX,{"derivedFrom":[subQ1,subQ0]});Q12=makeQuery(id+"F0.imprint","IMPRINT",FACE,{"disambiguationData":[TD([[makeQuery(id+"F0.imprint","IMPRINT",EDGE,{"disambiguationData":[TD([[subQ2,-1.0]])],"derivedFrom":subQ1}),-1.0]])]});}
            var Q13;
            {var subQ0=sQuery(id+"F0.wireOp",EDGE,"E28.bottom");var subQ1=sQuery(id+"F0.wireOp",EDGE,"E11.1.3.0");var subQ2=makeQuery(id+"F0.imprint","INTERSECT",VERTEX,{"derivedFrom":[subQ1,subQ0]});Q13=makeQuery(id+"F0.imprint","IMPRINT",FACE,{"disambiguationData":[TD([[makeQuery(id+"F0.imprint","IMPRINT",EDGE,{"disambiguationData":[TD([[subQ2,-1.0]])],"derivedFrom":subQ1}),1.0]])]});}
            var Q14;
            {var subQ4=sQuery(id+"F0.wireOp",EDGE,"E35.2");var subQ6=sQuery(id+"F0.wireOp",EDGE,"E11.1.3.0");var subQ8=makeQuery(id+"F0.imprint","INTERSECT",VERTEX,{"derivedFrom":[subQ6,subQ4]});Q14=makeQuery(id+"F0.imprint","IMPRINT",FACE,{"disambiguationData":[TD([[makeQuery(id+"F0.imprint","IMPRINT",EDGE,{"disambiguationData":[TD([[subQ8,-1.0]])],"derivedFrom":subQ6}),1.0]])]});}
            var Q15;
            {var subQ0=sQuery(id+"F0.wireOp",EDGE,"E29.left");var subQ1=sQuery(id+"F0.wireOp",EDGE,"E11.1.3.0");var subQ2=makeQuery(id+"F0.imprint","INTERSECT",VERTEX,{"disambiguationData":[OD(1.0)],"derivedFrom":[subQ1,subQ0]});Q15=makeQuery(id+"F0.imprint","IMPRINT",FACE,{"disambiguationData":[TD([[makeQuery(id+"F0.imprint","IMPRINT",EDGE,{"disambiguationData":[TD([[subQ2,-1.0]])],"derivedFrom":subQ1}),1.0]])]});}
            var Q16;
            {var subQ0=sQuery(id+"F0.wireOp",EDGE,"E28.left");var subQ1=sQuery(id+"F0.wireOp",EDGE,"E5");var subQ2=makeQuery(id+"F0.imprint","INTERSECT",VERTEX,{"derivedFrom":[subQ1,subQ0]});Q16=makeQuery(id+"F0.imprint","IMPRINT",FACE,{"disambiguationData":[TD([[makeQuery(id+"F0.imprint","IMPRINT",EDGE,{"disambiguationData":[TD([[subQ2,-1.0]])],"derivedFrom":subQ1}),-1.0]])]});}
            extrude(context, id + "F3", {"entities" : qUnion([Q0, Q1, Q2, Q3, Q4, Q5, Q6, Q7, Q8, Q9, Q10, Q11, Q12, Q13, Q14, Q15, Q16]), "operationType" : NewBodyOperationType.REMOVE, "depth" : 10 * mm, "offsetDistance" : 25 * mm});
        }
        {
            var Q0;
            {var subQ0=sQuery(id+"F0.wireOp",EDGE,"E8");var subQ1=sQuery(id+"F0.wireOp",EDGE,"E6");var subQ2=makeQuery(id+"F0.imprint","INTERSECT",VERTEX,{"derivedFrom":[subQ1,subQ0]});Q0=makeQuery(id+"F0.imprint","IMPRINT",FACE,{"disambiguationData":[TD([[makeQuery(id+"F0.imprint","IMPRINT",EDGE,{"disambiguationData":[TD([[subQ2,1.0]])],"derivedFrom":subQ1}),1.0]])]});}
            var Q1;
            {var subQ1=sQuery(id+"F0.wireOp",EDGE,"E8");var subQ14=sQuery(id+"F0.wireOp",EDGE,"E6");var subQ18=makeQuery(id+"F0.imprint","INTERSECT",VERTEX,{"derivedFrom":[subQ14,subQ1]});Q1=makeQuery(id+"F0.imprint","IMPRINT",FACE,{"disambiguationData":[TD([[makeQuery(id+"F0.imprint","IMPRINT",EDGE,{"disambiguationData":[TD([[subQ18,-1.0]])],"derivedFrom":subQ14}),1.0]])]});}
            var Q2;
            {var subQ1=sQuery(id+"F0.wireOp",EDGE,"E6");var subQ5=makeQuery(id+"F0.imprint","INTERSECT",VERTEX,{"derivedFrom":[subQ1,sQuery(id+"F0.wireOp",EDGE,"E8")]});Q2=makeQuery(id+"F0.imprint","IMPRINT",FACE,{"disambiguationData":[TD([[makeQuery(id+"F0.imprint","IMPRINT",EDGE,{"disambiguationData":[TD([[subQ5,1.0]])],"derivedFrom":subQ1}),-1.0]])]});}
            var Q3;
            {var subQ1=sQuery(id+"F0.wireOp",EDGE,"E6");var subQ3=sQuery(id+"F0.wireOp",EDGE,"E19.0");var subQ4=makeQuery(id+"F0.imprint","INTERSECT",VERTEX,{"derivedFrom":[subQ1,subQ3]});Q3=makeQuery(id+"F0.imprint","IMPRINT",FACE,{"disambiguationData":[TD([[makeQuery(id+"F0.imprint","IMPRINT",EDGE,{"disambiguationData":[TD([[subQ4,1.0]])],"derivedFrom":subQ3}),1.0]])]});}
            var Q4;
            {var subQ0=sQuery(id+"F0.wireOp",EDGE,"E6");var subQ5=sQuery(id+"F0.wireOp",EDGE,"E20.0");var subQ7=makeQuery(id+"F0.imprint","INTERSECT",VERTEX,{"derivedFrom":[subQ0,subQ5]});Q4=makeQuery(id+"F0.imprint","IMPRINT",FACE,{"disambiguationData":[TD([[makeQuery(id+"F0.imprint","IMPRINT",EDGE,{"disambiguationData":[TD([[subQ7,-1.0]])],"derivedFrom":subQ5}),1.0]])]});}
            var Q5;
            {var subQ3=sQuery(id+"F0.wireOp",EDGE,"E43.0");var subQ5=sQuery(id+"F0.wireOp",EDGE,"E42.0");var subQ6=makeQuery(id+"F0.imprint","INTERSECT",VERTEX,{"derivedFrom":[subQ5,subQ3]});Q5=makeQuery(id+"F0.imprint","IMPRINT",FACE,{"disambiguationData":[TD([[makeQuery(id+"F0.imprint","IMPRINT",EDGE,{"disambiguationData":[TD([[subQ6,-1.0]])],"derivedFrom":subQ5}),1.0]])]});}
            var Q6;
            {var subQ1=sQuery(id+"F0.wireOp",EDGE,"E5");var subQ3=sQuery(id+"F0.wireOp",EDGE,"E43.0");var subQ4=makeQuery(id+"F0.imprint","INTERSECT",VERTEX,{"derivedFrom":[subQ1,subQ3]});Q6=makeQuery(id+"F0.imprint","IMPRINT",FACE,{"disambiguationData":[TD([[makeQuery(id+"F0.imprint","IMPRINT",EDGE,{"disambiguationData":[TD([[subQ4,-1.0]])],"derivedFrom":subQ3}),1.0]])]});}
            var Q7;
            {var subQ0=sQuery(id+"F0.wireOp",EDGE,"E21");var subQ5=sQuery(id+"F0.wireOp",EDGE,"E42.0");var subQ6=makeQuery(id+"F0.imprint","INTERSECT",VERTEX,{"derivedFrom":[subQ0,subQ5]});Q7=makeQuery(id+"F0.imprint","IMPRINT",FACE,{"disambiguationData":[TD([[makeQuery(id+"F0.imprint","IMPRINT",EDGE,{"disambiguationData":[TD([[subQ6,-1.0]])],"derivedFrom":subQ5}),1.0]])]});}
            var Q8;
            {var subQ3=sQuery(id+"F0.wireOp",EDGE,"E41.0");var subQ5=sQuery(id+"F0.wireOp",EDGE,"E42.0");var subQ7=makeQuery(id+"F0.imprint","INTERSECT",VERTEX,{"derivedFrom":[subQ3,subQ5]});Q8=makeQuery(id+"F0.imprint","IMPRINT",FACE,{"disambiguationData":[TD([[makeQuery(id+"F0.imprint","IMPRINT",EDGE,{"disambiguationData":[TD([[subQ7,1.0]])],"derivedFrom":subQ3}),-1.0]])]});}
            var Q9;
            {var subQ4=sQuery(id+"F0.wireOp",EDGE,"E3");var subQ6=sQuery(id+"F0.wireOp",EDGE,"E41.0");var subQ7=makeQuery(id+"F0.imprint","INTERSECT",VERTEX,{"derivedFrom":[subQ4,subQ6]});Q9=makeQuery(id+"F0.imprint","IMPRINT",FACE,{"disambiguationData":[TD([[makeQuery(id+"F0.imprint","IMPRINT",EDGE,{"disambiguationData":[TD([[subQ7,-1.0]])],"derivedFrom":subQ6}),-1.0]])]});}
            extrude(context, id + "F4", {"entities" : qUnion([Q0, Q1, Q2, Q3, Q4, Q5, Q6, Q7, Q8, Q9]), "operationType" : NewBodyOperationType.REMOVE, "depth" : 10 * mm, "offsetDistance" : 25 * mm});
        }
        {
            var Q0;
            {var subQ0=sQuery(id+"F0.wireOp",EDGE,"E15");var subQ1=makeQuery(id+"F0.imprint","INTERSECT",VERTEX,{"derivedFrom":[sQuery(id+"F0.wireOp",EDGE,"E5"),subQ0]});var subQ2=makeQuery(id+"F0.imprint","INTERSECT",VERTEX,{"derivedFrom":[subQ0,sQuery(id+"F0.wireOp",EDGE,"E42.0")]});Q0=makeQuery(id+"F1.opExtrude","CAP_EDGE",EDGE,{"disambiguationData":[OSD([subQ0]),TDD([makeQuery(id+"F0.imprint","IMPRINT",EDGE,{"disambiguationData":[TD([[subQ2,1.0]])],"derivedFrom":subQ0}),makeQuery(id+"F0.imprint","IMPRINT",EDGE,{"disambiguationData":[TD([[subQ1,1.0]])],"derivedFrom":subQ0}),makeQuery(id+"F0.imprint","IMPRINT",EDGE,{"disambiguationData":[TD([[makeQuery(id+"F0.imprint","INTERSECT",VERTEX,{"derivedFrom":[subQ0,sQuery(id+"F0.wireOp",EDGE,"E20.0")]}),1.0]])],"derivedFrom":subQ0})])],"isStart":false});}
            var Q1;
            {var subQ0=sQuery(id+"F0.wireOp",EDGE,"E15");Q1=makeQuery(id+"F1.opExtrude","CAP_EDGE",EDGE,{"disambiguationData":[OSD([subQ0]),TDD([makeQuery(id+"F0.imprint","IMPRINT",EDGE,{"disambiguationData":[TD([[makeQuery(id+"F0.imprint","INTERSECT",VERTEX,{"derivedFrom":[subQ0,sQuery(id+"F0.wireOp",EDGE,"E19.0")]}),-1.0]])],"derivedFrom":subQ0})])],"isStart":false});}
            chamfer(context, id + "F5", {"entities" : qUnion([Q0, Q1]), "width" : 7 * mm, "tangentPropagation" : true});
        }
        {
            var Q0;
            Q0=makeQuery(id+"F2.opExtrude","CAP_EDGE",EDGE,{"disambiguationData":[OSD([sQuery(id+"F0.wireOp",EDGE,"E30")])],"isStart":false});
            var Q1;
            Q1=makeQuery(id+"F2.opExtrude","CAP_EDGE",EDGE,{"disambiguationData":[OSD([sQuery(id+"F0.wireOp",EDGE,"E17")])],"isStart":false});
            chamfer(context, id + "F6", {"entities" : qUnion([Q0, Q1]), "width" : 2 * mm, "tangentPropagation" : true});
        }
        {
            var Q0;
            Q0=makeQuery(id+"F1.opExtrude","SWEPT_EDGE",EDGE,{"disambiguationData":[OSD([sQuery(id+"F0.wireOp",EDGE,"E3"),sQuery(id+"F0.wireOp",EDGE,"E34")])]});
            fillet(context, id + "F7", {"entities" : qUnion([Q0]), "radius" : 5 * mm, "tangentPropagation" : true, "allowEdgeOverflow" : false});
        }
        {
            var Q0;
            Q0=makeQuery(id+"F1.opExtrude","SWEPT_BODY",BODY,{"disambiguationData":[OSD([sQuery(id+"F0.wireOp",EDGE,"E3"),sQuery(id+"F0.wireOp",EDGE,"E9"),sQuery(id+"F0.wireOp",EDGE,"E10.1.0"),sQuery(id+"F0.wireOp",EDGE,"E10.2.0"),sQuery(id+"F0.wireOp",EDGE,"E13.1.14.0"),sQuery(id+"F0.wireOp",EDGE,"E13.1.15.0"),sQuery(id+"F0.wireOp",EDGE,"E15"),sQuery(id+"F0.wireOp",EDGE,"E16"),sQuery(id+"F0.wireOp",EDGE,"E19.0"),sQuery(id+"F0.wireOp",EDGE,"E20.0"),sQuery(id+"F0.wireOp",EDGE,"E23"),sQuery(id+"F0.wireOp",EDGE,"E24"),sQuery(id+"F0.wireOp",EDGE,"E26"),sQuery(id+"F0.wireOp",EDGE,"E27"),sQuery(id+"F0.wireOp",EDGE,"E28.top"),sQuery(id+"F0.wireOp",EDGE,"E30"),sQuery(id+"F0.wireOp",EDGE,"E32"),sQuery(id+"F0.wireOp",EDGE,"E33"),sQuery(id+"F0.wireOp",EDGE,"E34"),sQuery(id+"F0.wireOp",EDGE,"E36.0"),sQuery(id+"F0.wireOp",EDGE,"E37"),sQuery(id+"F0.wireOp",EDGE,"E44.0")])]});
            var Q1;
            Q1=qCreatedBy(makeId("Right.planeOp"),FACE);
            mirror(context, id + "F8", {"entities" : qUnion([Q0]), "mirrorPlane" : qUnion([Q1])});
        }
    });
